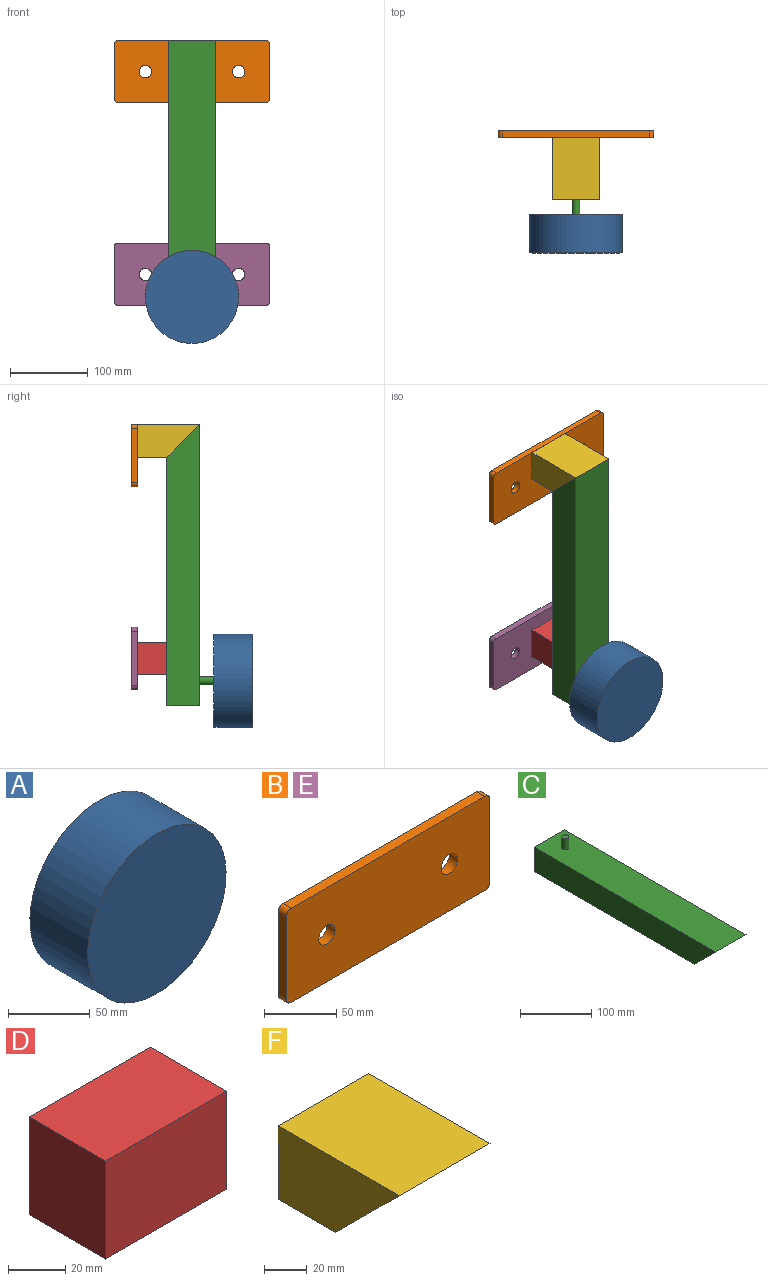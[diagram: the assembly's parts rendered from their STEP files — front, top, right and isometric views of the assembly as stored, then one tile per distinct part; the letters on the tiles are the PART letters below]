
ASSEMBLY  parts=6 mates=5
PART A: 3 faces, bbox 120x50x120 mm
  f0: cylinder r=60mm len=120mm, axis (0,1,0), area 18849.6mm2, adj f1,f2
  f1: plane 120x120mm, normal (0,-1,0), area 11309.7mm2, adj f0
  f2: plane 120x120mm, normal (0,1,0), area 11309.7mm2, adj f0
PART B: 12 faces, bbox 200x8x80 mm
  f0: plane 190x8mm, normal (0,0,1), area 1520mm2, adj f4,f5,f6,f9
  f1: plane 70x8mm, normal (-1,0,0), area 560mm2, adj f4,f5,f6,f7
  f2: plane 190x8mm, normal (0,0,-1), area 1520mm2, adj f4,f5,f7,f8
  f3: plane 70x8mm, normal (1,0,0), area 560mm2, adj f4,f5,f8,f9
  f4: plane 200x80mm, normal (0,-1,0), area 15576.4mm2, adj f0,f1,f2,f3,f6,f7,f8,f9
  f5: plane 200x80mm, normal (0,1,0), area 15576.4mm2, adj f0,f1,f2,f3,f6,f7,f8,f9
  f6: cylinder r=5mm len=8mm, axis (0,-1,0), area 62.8mm2, adj f0,f1,f4,f5
  f7: cylinder r=5mm len=8mm, axis (0,1,0), area 62.8mm2, adj f1,f2,f4,f5
  f8: cylinder r=5mm len=8mm, axis (0,-1,0), area 62.8mm2, adj f2,f3,f4,f5
  f9: cylinder r=5mm len=8mm, axis (0,1,0), area 62.8mm2, adj f0,f3,f4,f5
  f10: cylinder r=8mm len=16mm, axis (0,-1,0), area 402.1mm2, adj f4,f5
  f11: cylinder r=8mm len=16mm, axis (0,-1,0), area 402.1mm2, adj f4,f5
PART C: 8 faces, bbox 60x362x60.5 mm
  f0: plane 320x60mm, normal (0,0,-1), area 19200mm2, adj f1,f2,f4,f5
  f1: plane 362x42mm, normal (-1,0,0), area 14322mm2, adj f0,f3,f4,f5
  f2: plane 362x42mm, normal (1,0,0), area 14322mm2, adj f0,f3,f4,f5
  f3: plane 362x60mm, normal (0,0,1), area 21641.5mm2, adj f1,f2,f4,f5,f6
  f4: plane 60x42mm, normal (0,1,0), area 2520mm2, adj f0,f1,f2,f3
  f5: plane 60x42mm, normal (0,-0.71,-0.71), area 3563.8mm2, adj f0,f1,f2,f3
  f6: cylinder r=5mm len=18.5mm, axis (0,0,-1), area 581.2mm2, adj f3,f7
  f7: plane 10x10mm, normal (0,0,1), area 78.5mm2, adj f6
PART D: 6 faces, bbox 60x38x42 mm
  f0: plane 42x38mm, normal (-1,0,0), area 1596mm2, adj f1,f3,f4,f5
  f1: plane 60x38mm, normal (0,0,-1), area 2280mm2, adj f0,f2,f4,f5
  f2: plane 42x38mm, normal (1,0,0), area 1596mm2, adj f1,f3,f4,f5
  f3: plane 60x38mm, normal (0,0,1), area 2280mm2, adj f0,f2,f4,f5
  f4: plane 60x42mm, normal (0,-1,0), area 2520mm2, adj f0,f1,f2,f3
  f5: plane 60x42mm, normal (0,1,0), area 2520mm2, adj f0,f1,f2,f3
PART E: same geometry as B
PART F: 6 faces, bbox 60x80x42 mm
  f0: plane 60x38mm, normal (0,0,-1), area 2280mm2, adj f1,f2,f4,f5
  f1: plane 80x42mm, normal (-1,0,0), area 2478mm2, adj f0,f3,f4,f5
  f2: plane 80x42mm, normal (1,0,0), area 2478mm2, adj f0,f3,f4,f5
  f3: plane 80x60mm, normal (0,0,1), area 4800mm2, adj f1,f2,f4,f5
  f4: plane 60x42mm, normal (0,1,0), area 2520mm2, adj f0,f1,f2,f3
  f5: plane 60x42mm, normal (0,-0.71,-0.71), area 3563.8mm2, adj f0,f1,f2,f3
PLACE A at identity
PLACE B t=(0,106.5,290)mm
PLACE C rot(axis=(0,-0.71,0.71),180deg) t=(30,60.5,-32)mm
PLACE D rot(axis=(0,1,0),180deg) t=(30,98.5,50)mm
PLACE E t=(0,106.5,29)mm
PLACE F t=(-30,98.5,288)mm
MATE fastened F.f5 <-> C.f5  axis (0,-0.71,-0.71) through (0,39.5,309)mm
MATE fastened D.f4 <-> C.f0  axis (0,-1,0) through (0,60.5,29)mm
MATE fastened C.f6 <-> A.f0  axis (0,-1,0) through (0,0,0)mm
MATE fastened B.f4 <-> F.f4  axis (0,-1,0) through (0,98.5,330)mm
MATE fastened E.f4 <-> D.f5  axis (0,-1,0) through (0,98.5,29)mm
